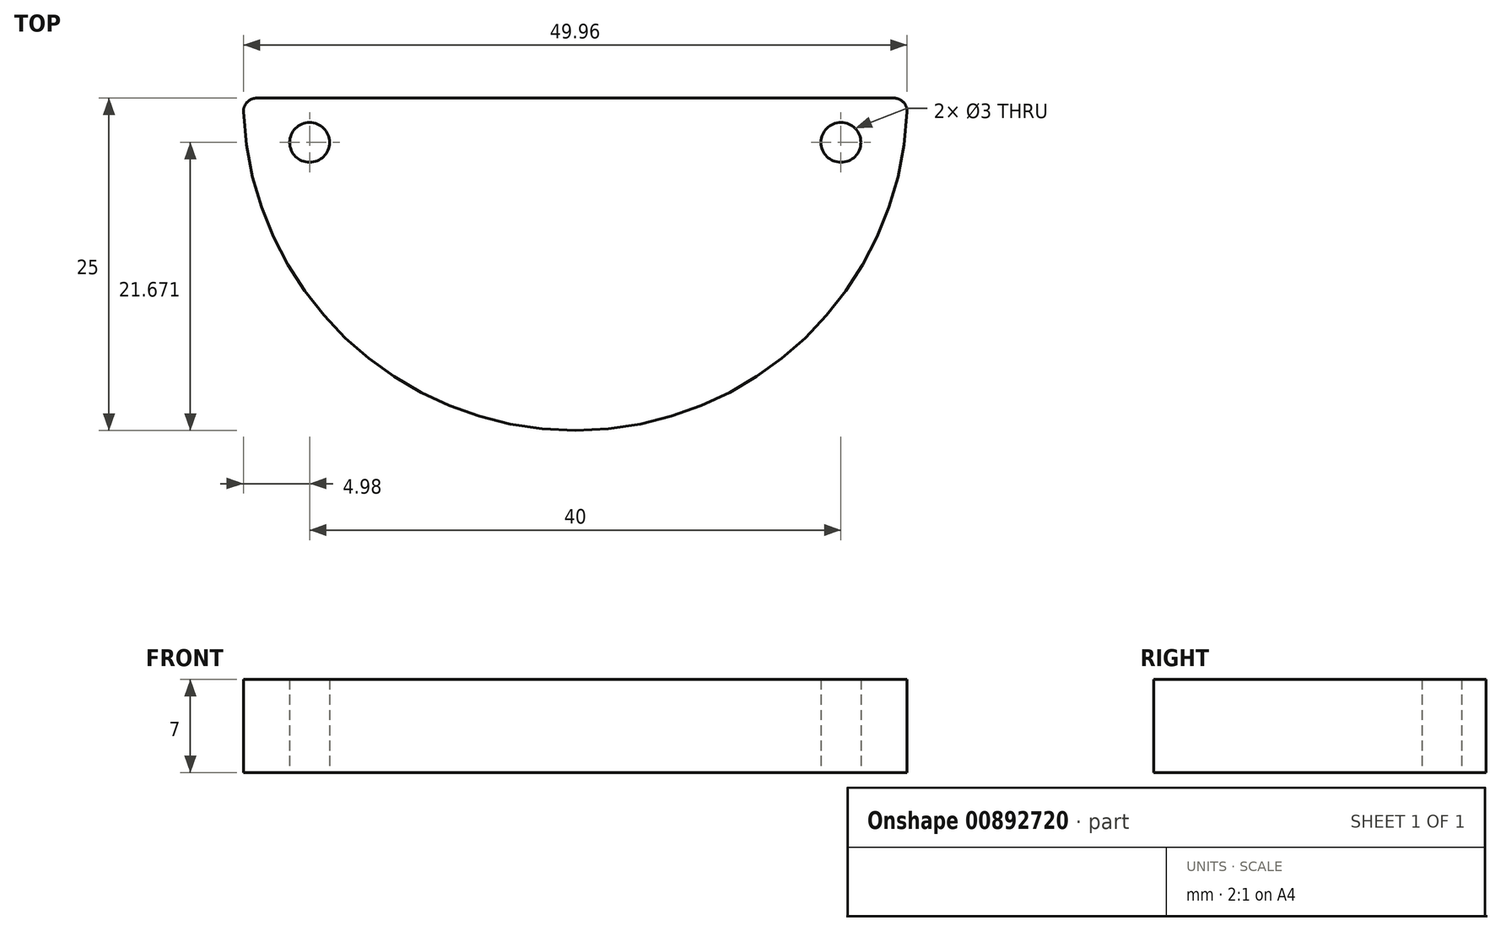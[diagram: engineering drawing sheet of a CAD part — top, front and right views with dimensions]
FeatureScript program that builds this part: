
annotation { "Feature Type Name" : "Feature", "Feature Type Description" : "" }
export const myFeature = defineFeature(function(context is Context, id is Id, definition is map)
    precondition{}
    {
        {
            var Q0;
            Q0=qCreatedBy(makeId("Top.planeOp"),FACE);
            var sketch = newSketch(context, id + "F0", { "sketchPlane" : qUnion([Q0])});
            skLineSegment(sketch, "E0", {"start": v(0, 0) * mm, "end": v(0, -25) * mm});
            skArc(sketch, "E1", {"start": v(0, -25) * mm, "mid": v(-17.68, -17.68) * mm, "end": v(-25, 0) * mm});
            skArc(sketch, "E2", {"start": v(0, -25) * mm, "mid": v(17.68, -17.68) * mm, "end": v(25, 0) * mm});
            skLineSegment(sketch, "E3", {"start": v(-25, 0) * mm, "end": v(25, 0) * mm});
            skCircle(sketch, "E4", {"center": v(-20, -3.33) * mm, "radius": 1.5 * mm});
            skCircle(sketch, "E5", {"center": v(20, -3.33) * mm, "radius": 1.5 * mm});
            skSolve(sketch);
        }
        {
            var Q0;
            Q0 = qSketchRegion(id + "F0", true);
            extrude(context, id + "F1", {"entities" : qUnion([Q0]), "depth" : 7 * mm, "offsetDistance" : 25 * mm});
        }
        {
            var Q0;
            Q0=makeQuery(id+"F1.opExtrude","SWEPT_EDGE",EDGE,{"disambiguationData":[OSD([sQuery(id+"F0.wireOp",EDGE,"E2"),sQuery(id+"F0.wireOp",EDGE,"E3")])]});
            var Q1;
            Q1=makeQuery(id+"F1.opExtrude","SWEPT_EDGE",EDGE,{"disambiguationData":[OSD([sQuery(id+"F0.wireOp",EDGE,"E1"),sQuery(id+"F0.wireOp",EDGE,"E3")])]});
            fillet(context, id + "F2", {"entities" : qUnion([Q0, Q1]), "radius" : 1 * mm, "tangentPropagation" : true, "allowEdgeOverflow" : false});
        }
    });
